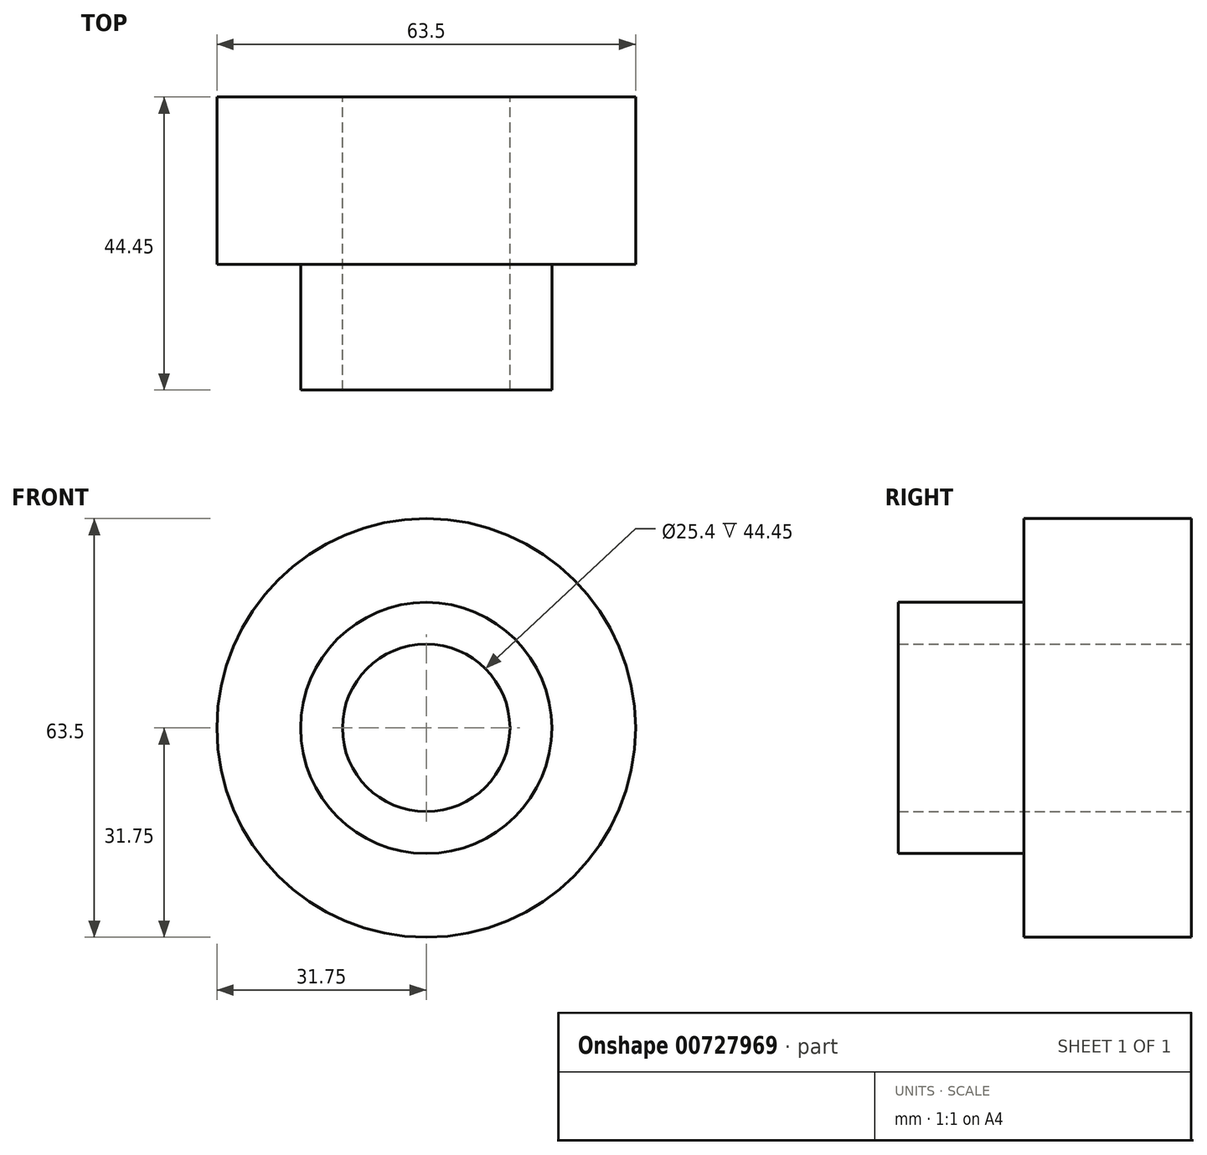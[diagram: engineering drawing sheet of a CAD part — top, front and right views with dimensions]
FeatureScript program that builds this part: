
annotation { "Feature Type Name" : "Feature", "Feature Type Description" : "" }
export const myFeature = defineFeature(function(context is Context, id is Id, definition is map)
    precondition{}
    {
        {
            var Q0;
            Q0=qCreatedBy(makeId("Front.planeOp"),FACE);
            var sketch = newSketch(context, id + "F0", { "sketchPlane" : qUnion([Q0])});
            skCircle(sketch, "E0", {"center": v(0, 0) * mm, "radius": 31.75 * mm});
            skSolve(sketch);
        }
        {
            var Q0;
            Q0=qCreatedBy(makeId("Front.planeOp"),FACE);
            var sketch = newSketch(context, id + "F1", { "sketchPlane" : qUnion([Q0])});
            skCircle(sketch, "E1", {"center": v(0, 0) * mm, "radius": 19.05 * mm});
            skCircle(sketch, "E2", {"center": v(0, 0) * mm, "radius": 12.7 * mm});
            skSolve(sketch);
        }
        {
            var Q0;
            Q0 = qSketchRegion(id + "F1", true);
            extrude(context, id + "F2", {"entities" : qUnion([Q0]), "depth" : 44.45 * mm, "offsetDistance" : 25.4 * mm});
        }
        {
            var Q0;
            Q0=makeQuery(id+"F0.imprint","IMPRINT",FACE,{"disambiguationData":[TD([[makeQuery(id+"F0.imprint","IMPRINT",EDGE,{"derivedFrom":sQuery(id+"F0.wireOp",EDGE,"E0")}),1.0]])]});
            extrude(context, id + "F3", {"entities" : qUnion([Q0]), "operationType" : NewBodyOperationType.ADD, "depth" : 25.4 * mm, "offsetDistance" : 25.4 * mm});
        }
        {
            var Q0;
            Q0=makeQuery(id+"F3.boolean.opBoolean","SPLIT",FACE,{"disambiguationData":[TD([makeQuery(id+"F2.opExtrude","SWEPT_FACE",FACE,{"disambiguationData":[OSD([sQuery(id+"F1.wireOp",EDGE,"E2")])]})])],"derivedFrom":makeQuery(id+"F3.opExtrude","CAP_FACE",FACE,{"disambiguationData":[OSD([sQuery(id+"F0.wireOp",EDGE,"E0")])],"isStart":false})});
            extrude(context, id + "F4", {"entities" : qUnion([Q0]), "operationType" : NewBodyOperationType.REMOVE, "oppositeDirection" : true, "depth" : 25.4 * mm, "offsetDistance" : 25.4 * mm});
        }
    });
